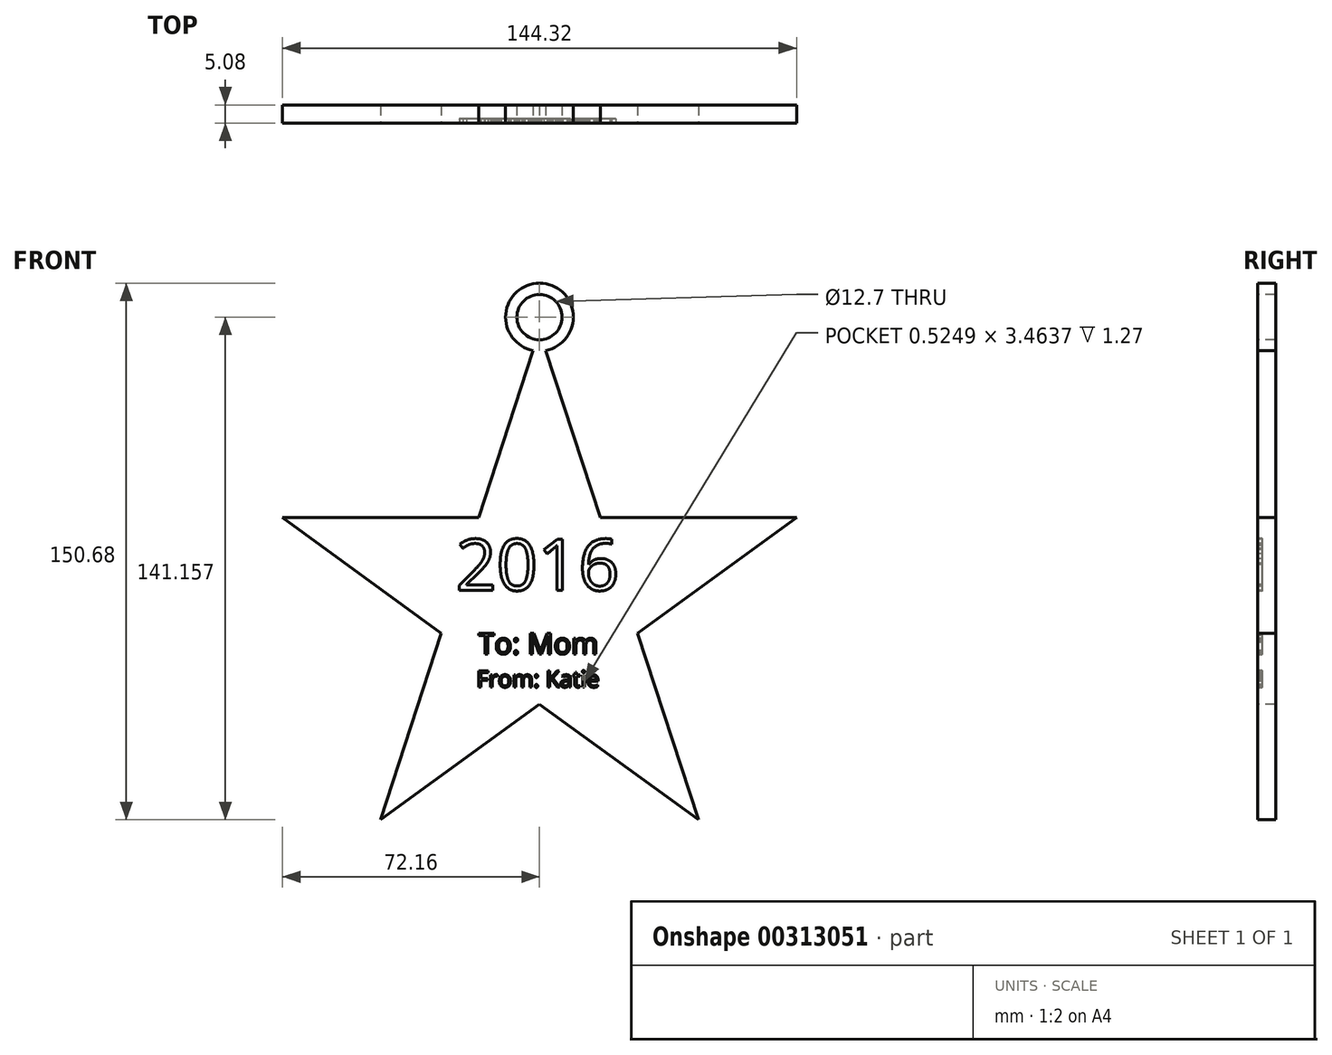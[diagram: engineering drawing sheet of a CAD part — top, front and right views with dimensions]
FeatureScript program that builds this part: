
annotation { "Feature Type Name" : "Feature", "Feature Type Description" : "" }
export const myFeature = defineFeature(function(context is Context, id is Id, definition is map)
    precondition{}
    {
        {
            var Q0;
            Q0=qCreatedBy(makeId("Front.planeOp"),FACE);
            var sketch = newSketch(context, id + "F0", { "sketchPlane" : qUnion([Q0])});
            skLineSegment(sketch, "E0", {"start": v(-17.03, 23.45) * mm, "end": v(0, 0) * mm});
            skLineSegment(sketch, "E1", {"start": v(0, 0) * mm, "end": v(17.03, 23.45) * mm});
            skLineSegment(sketch, "E2", {"start": v(0, 0) * mm, "end": v(27.56, -8.96) * mm});
            skLineSegment(sketch, "E3", {"start": v(-27.56, -8.96) * mm, "end": v(0, 0) * mm});
            skLineSegment(sketch, "E4", {"start": v(0, -28.98) * mm, "end": v(0, 0) * mm});
            skLineSegment(sketch, "E5", {"start": v(-72.16, 23.45) * mm, "end": v(-17.03, 23.45) * mm});
            skLineSegment(sketch, "E6", {"start": v(17.03, 23.45) * mm, "end": v(72.16, 23.45) * mm});
            skLineSegment(sketch, "E7", {"start": v(-72.16, 23.45) * mm, "end": v(-27.56, -8.96) * mm});
            skLineSegment(sketch, "E8", {"start": v(44.6, -61.38) * mm, "end": v(0, -28.98) * mm});
            skLineSegment(sketch, "E9", {"start": v(-17.03, 23.45) * mm, "end": v(0, 75.87) * mm});
            skLineSegment(sketch, "E10", {"start": v(-27.56, -8.96) * mm, "end": v(-44.6, -61.38) * mm});
            skLineSegment(sketch, "E11", {"start": v(0, 75.87) * mm, "end": v(17.03, 23.45) * mm});
            skLineSegment(sketch, "E12", {"start": v(27.56, -8.96) * mm, "end": v(44.6, -61.38) * mm});
            skLineSegment(sketch, "E13", {"start": v(72.16, 23.45) * mm, "end": v(27.56, -8.96) * mm});
            skLineSegment(sketch, "E14", {"start": v(0, -28.98) * mm, "end": v(-44.6, -61.38) * mm});
            skSolve(sketch);
        }
        {
            var Q0;
            Q0 = qSketchRegion(id + "F0", true);
            extrude(context, id + "F1", {"entities" : qUnion([Q0]), "oppositeDirection" : true, "depth" : 5.08 * mm});
        }
        {
            var Q0;
            Q0=qCreatedBy(makeId("Front.planeOp"),FACE);
            var sketch = newSketch(context, id + "F2", { "sketchPlane" : qUnion([Q0])});
            skText(sketch, "E15", { "text": "From: Katie", "fontName": "OpenSans-Regular.ttf"});
            skText(sketch, "E16", { "text": "To: Mom", "fontName": "OpenSans-Regular.ttf"});
            skText(sketch, "E17", { "text": "2016", "fontName": "OpenSans-Regular.ttf"});
            const initialGuessF2  = {"E15": [-0.01764, -0.02414, 1, 0, 0.00466], "E16": [-0.01715, -0.01483, 1, 0, 0.00588], "E17": [-0.02353, 0.00306, 1, 0, 0.01446]};
            skSetInitialGuess(sketch, initialGuessF2);
            skSolve(sketch);
        }
        {
            var Q0;
            Q0 = qSketchRegion(id + "F2", true);
            extrude(context, id + "F3", {"entities" : qUnion([Q0]), "operationType" : NewBodyOperationType.REMOVE, "oppositeDirection" : true, "depth" : 1.27 * mm});
        }
        {
            var Q0;
            Q0=qCreatedBy(makeId("Front.planeOp"),FACE);
            var sketch = newSketch(context, id + "F4", { "sketchPlane" : qUnion([Q0])});
            skCircle(sketch, "E18", {"center": v(0, 79.78) * mm, "radius": 9.53 * mm});
            skSolve(sketch);
        }
        {
            var Q0;
            Q0 = qSketchRegion(id + "F4", true);
            extrude(context, id + "F5", {"entities" : qUnion([Q0]), "operationType" : NewBodyOperationType.ADD, "oppositeDirection" : true, "depth" : 5.08 * mm});
        }
        {
            var Q0;
            Q0=qCreatedBy(makeId("Front.planeOp"),FACE);
            var sketch = newSketch(context, id + "F6", { "sketchPlane" : qUnion([Q0])});
            skCircle(sketch, "E19", {"center": v(0, 79.78) * mm, "radius": 6.35 * mm});
            skSolve(sketch);
        }
        {
            var Q0;
            Q0 = qSketchRegion(id + "F6", true);
            extrude(context, id + "F7", {"entities" : qUnion([Q0]), "operationType" : NewBodyOperationType.REMOVE, "oppositeDirection" : true, "depth" : 5.08 * mm});
        }
    });
